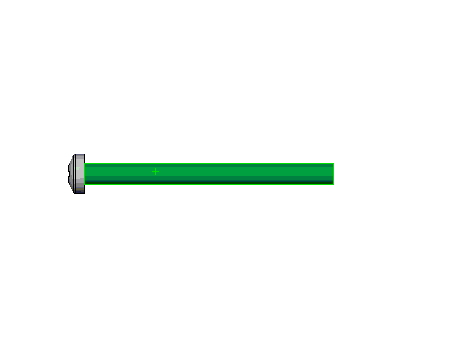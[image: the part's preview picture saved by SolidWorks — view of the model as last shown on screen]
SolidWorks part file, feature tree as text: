
SOLIDWORKS PART (.sldprt)
format: sldprt  version: not decoded by parser v0  size: 184,320 bytes
history: native  units: mm
features: plane x4, sketch x4, cut_revolve x4, material x1, revolve x1, thread x1, pattern_circular x1, pattern_linear x1 (+11 scaffold rows collapsed; 1 parser-record rows omitted)
feature tree (29):
  parser-record x1  (decoder bookkeeping rows leaked as tree rows — omitted from the tree; the rows remain in map.json)
  scaffold x11  (default folders/planes/origin — collapsed)
  material  "Material <not specified>"
  plane  "Plane1"
  plane  "Plane2"
  plane  "Plane3"
  sketch  "BodySke"  dims[c1.Head_fillet_rad=3.6322mm c1.Head_crown_rad=5.0mm c2.Head_fillet_rad=0.36mm c2.D1=~7.099516mm c2.Head_ang=85.0deg c2.Oval_ht=2.3876mm c2.Head_ht=6.1976mm c2.Diameter=3.0mm c2.Length=76.2mm c2.Head_dia=20.0152mm c3.Head_dia=15.3924mm c3.Head_ht=8.509mm c3.Length=35.0mm c3.Head_side_ht=6.1722mm c4.Head_ht=5.1562mm c4.Head_dia=18.4912mm c5.Head_ht=2.4mm c5.Head_dia=5.6mm c5.Advance=0.5mm c5.Thread_nom=30.0mm c5.Thread_lim=~37.30625mm]
  revolve  "Base-Revolve"  [1 undecoded]
  thread  "ThreadCosmetic"  Diameter=30mm Thread_length=30mm Thread_minor=2.439mm Head_dia=5.6mm  [1 undecoded]
  sketch  "Sketch3"  dims[Cross_dia=2.9mm D1=1.45mm Cross_width=0.74mm D2=0.37mm]
  plane  "Plane4"  Offset=1.76mm Cross_depth=1.76mm
  sketch  "Sketch4"  dims[D1=0.37mm D2=0.37mm D3=0.185mm D4=0.185mm]
  pattern_circular  "CirPattern1"  Count=2 Angle=90deg
  sketch  "ThdSchSke"  dims[c1.Thread_minor=~1.03886mm c1.Diameter=~1.413535mm c1.Start=~0.988134mm c1.D4=~4.446753mm c1.Vee=60.0deg c2.Thread_minor=~1.03886mm c2.Start=~2.540025mm c2.D1=~0.108159mm c2.D2=~0.108159mm c3.D1=~0.216319mm c3.SideAngle=55.0deg c3.D2=~0.216319mm c3.VeeAngle=70.0deg c3.Thread_minor=2.439mm c3.Overcut=3.75mm c3.Diameter=3.0mm c3.D6=~8.326268mm c4.D1=~8.326268mm c5.D1=90.0deg c5.Start=11.1125mm c6.Start=~44.450025mm c7.Start=7.4mm]
  cut_revolve  "ThreadSchematic"  Angle=360deg
  pattern_linear  "ThdSchPat"  Count1=61 Count2=1 Spacing1=0.5mm Spacing2=50mm Num_threads=61 Advance=0.5mm
  cut_revolve  "ConfigurationName"  CopiedFlag=1  [1 undecoded]
  cut_revolve  "PartNumberID"  [1 undecoded]
  cut_revolve  "ConfigurationName"  CopiedFlag=0  [1 undecoded]
decode coverage: 10 of 12 modeling features carry decoded parameters
note: ~ marks probable driven/reference dimensions
note: 5 parameter values undecoded
summary: no parameter record found for 4 features
note: suppression state not decoded; provenance and decode notes live in map.json
